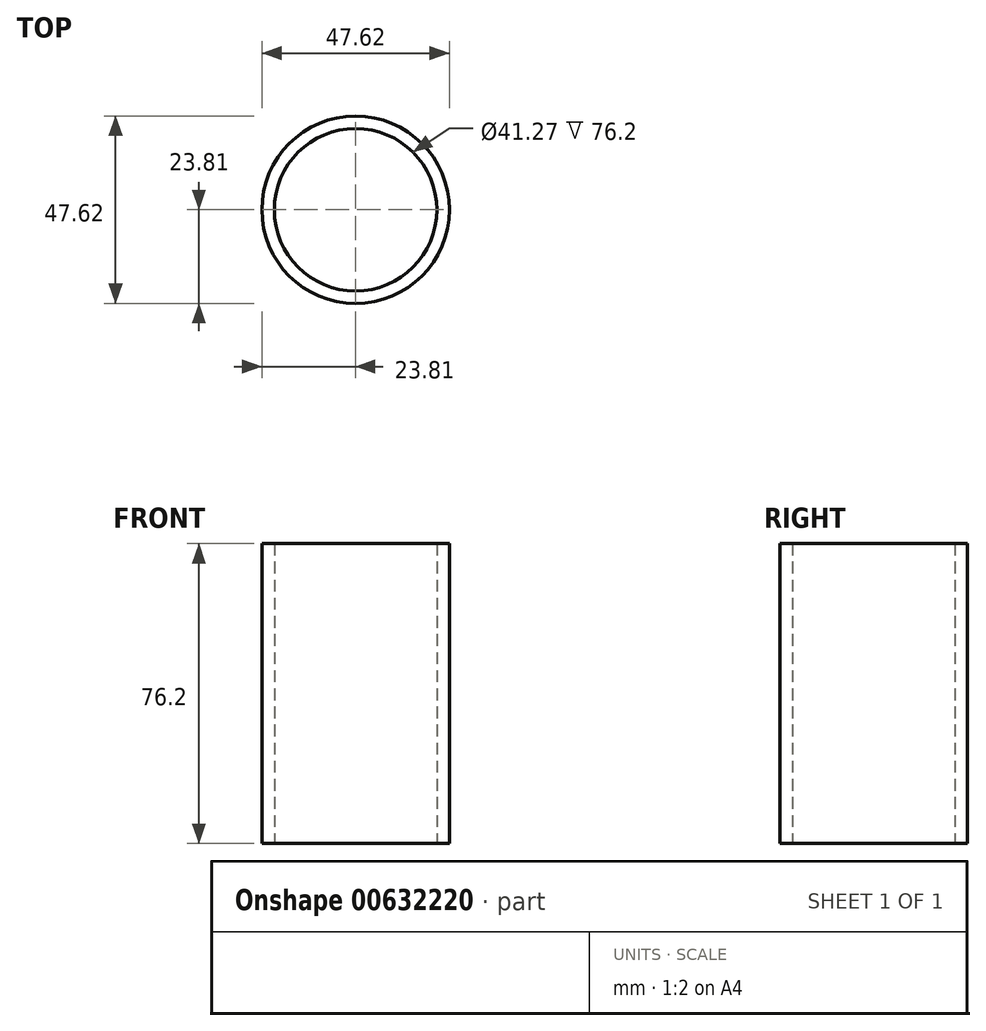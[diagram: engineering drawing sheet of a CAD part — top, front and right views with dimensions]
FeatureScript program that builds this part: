
annotation { "Feature Type Name" : "Feature", "Feature Type Description" : "" }
export const myFeature = defineFeature(function(context is Context, id is Id, definition is map)
    precondition{}
    {
        {
            var Q0;
            Q0=qCreatedBy(makeId("Top.planeOp"),FACE);
            var sketch = newSketch(context, id + "F0", { "sketchPlane" : qUnion([Q0])});
            skCircle(sketch, "E0", {"center": v(0, 0) * mm, "radius": 20.64 * mm});
            skCircle(sketch, "E1.0", {"center": v(0, 0) * mm, "radius": 23.81 * mm});
            skSolve(sketch);
        }
        {
            var Q0;
            Q0=makeQuery(id+"F0.imprint","IMPRINT",FACE,{"disambiguationData":[TD([[makeQuery(id+"F0.imprint","IMPRINT",EDGE,{"derivedFrom":sQuery(id+"F0.wireOp",EDGE,"E0")}),-1.0]])]});
            extrude(context, id + "F1", {"entities" : qUnion([Q0]), "depth" : 76.2 * mm, "offsetDistance" : 25.4 * mm});
        }
    });
